# Revit family: КРД
name_source: partatom
category: Оборудование
units: mm (PartAtom-declared; Revit-internal decimal feet)

## family parameters
Всегда вертикально = Да
Классификация = Нет
На основе рабочей плоскости = Нет
Общий = Нет
При загрузке вырезать с полостями = Нет
Размер круглого соединителя = Использовать диаметр
Тип детали = Нормальный
Точка принадлежности помещению = Нет

## types (25) — shared parameters
00_20_Manufacturer = Вентс
00_20_Name = Клапан регулювання тиску
Grid Material = Cover Grid Cross
L = 100 мм
Load Classification = HVAC
Maintenance zone material = <По категории>
Maximum Air Flow = 0.0 л/с
URL = https://vents.ua
zero-valued in all types: Отметка по умолчанию

## per-type parameters (varying)
| type | B | H | Hole | a | a1 | p1 | С правым фланем |
| КРД-1-1000х1000 | 1000 мм | 1000 мм | Да | 15 мм | 30 мм | 400 мм | Нет |
| КРД-1-425х425 | 425 мм | 425 мм | Да | 10 мм | 20 мм | 170 мм | Нет |
| КРД-1-300х300 | 300 мм | 300 мм | Нет | 10 мм | 20 мм | 120 мм | Нет |
| КРД-1-550х550 | 550 мм | 550 мм | Да | 15 мм | 30 мм | 220 мм | Нет |
| КРД-1-600х175 | 600 мм | 175 мм | Да | 10 мм | 20 мм | 70 мм | Нет |
| КРД-1-700х300 | 700 мм | 300 мм | Да | 10 мм | 20 мм | 120 мм | Нет |
| КРД-1-800х800 | 800 мм | 800 мм | Да | 15 мм | 30 мм | 320 мм | Нет |
| КРД-1-900х900 | 900 мм | 900 мм | Да | 15 мм | 30 мм | 360 мм | Нет |
| КРД-1-200х300 | 200 мм | 300 мм | Нет | 10 мм | 20 мм | 120 мм | Нет |
| КРД-1-300х175 | 300 мм | 175 мм | Нет | 10 мм | 20 мм | 70 мм | Нет |
| КРД-1-675х675 | 675 мм | 675 мм | Да | 15 мм | 30 мм | 270 мм | Нет |
| КРД-1-800х650 | 800 мм | 650 мм | Да | 15 мм | 30 мм | 260 мм | Нет |
| КРД-1-200х200 | 200 мм | 200 мм | Нет | 10 мм | 20 мм | 80 мм | Нет |
| КРД-2-200х200 | 200 мм | 200 мм | Нет | 10 мм | 20 мм | 80 мм | Да |
| КРД-2-300х300 | 300 мм | 300 мм | Нет | 10 мм | 20 мм | 120 мм | Да |
| КРД-2-400х400 | 400 мм | 400 мм | Да | 10 мм | 20 мм | 160 мм | Да |
| КРД-1-400х400 | 400 мм | 400 мм | Да | 10 мм | 20 мм | 160 мм | Нет |
| КРД-2-500х500 | 500 мм | 500 мм | Да | 10 мм | 20 мм | 200 мм | Да |
| КРД-1-500х500 | 500 мм | 500 мм | Да | 10 мм | 20 мм | 200 мм | Нет |
| КРД-2-600х600 | 600 мм | 600 мм | Да | 15 мм | 30 мм | 240 мм | Да |
| КРД-1-600х600 | 600 мм | 600 мм | Да | 15 мм | 30 мм | 240 мм | Нет |
| КРД-1-700х700 | 700 мм | 700 мм | Да | 15 мм | 30 мм | 280 мм | Нет |
| КРД-2-700х700 | 700 мм | 700 мм | Да | 15 мм | 30 мм | 280 мм | Да |
| КРД-2-800х800 | 800 мм | 800 мм | Да | 15 мм | 30 мм | 320 мм | Да |
| КРД-2-900х900 | 900 мм | 900 мм | Да | 15 мм | 30 мм | 360 мм | Да |

note: column(s) folded — value = type name in every type: 00_20_Type
